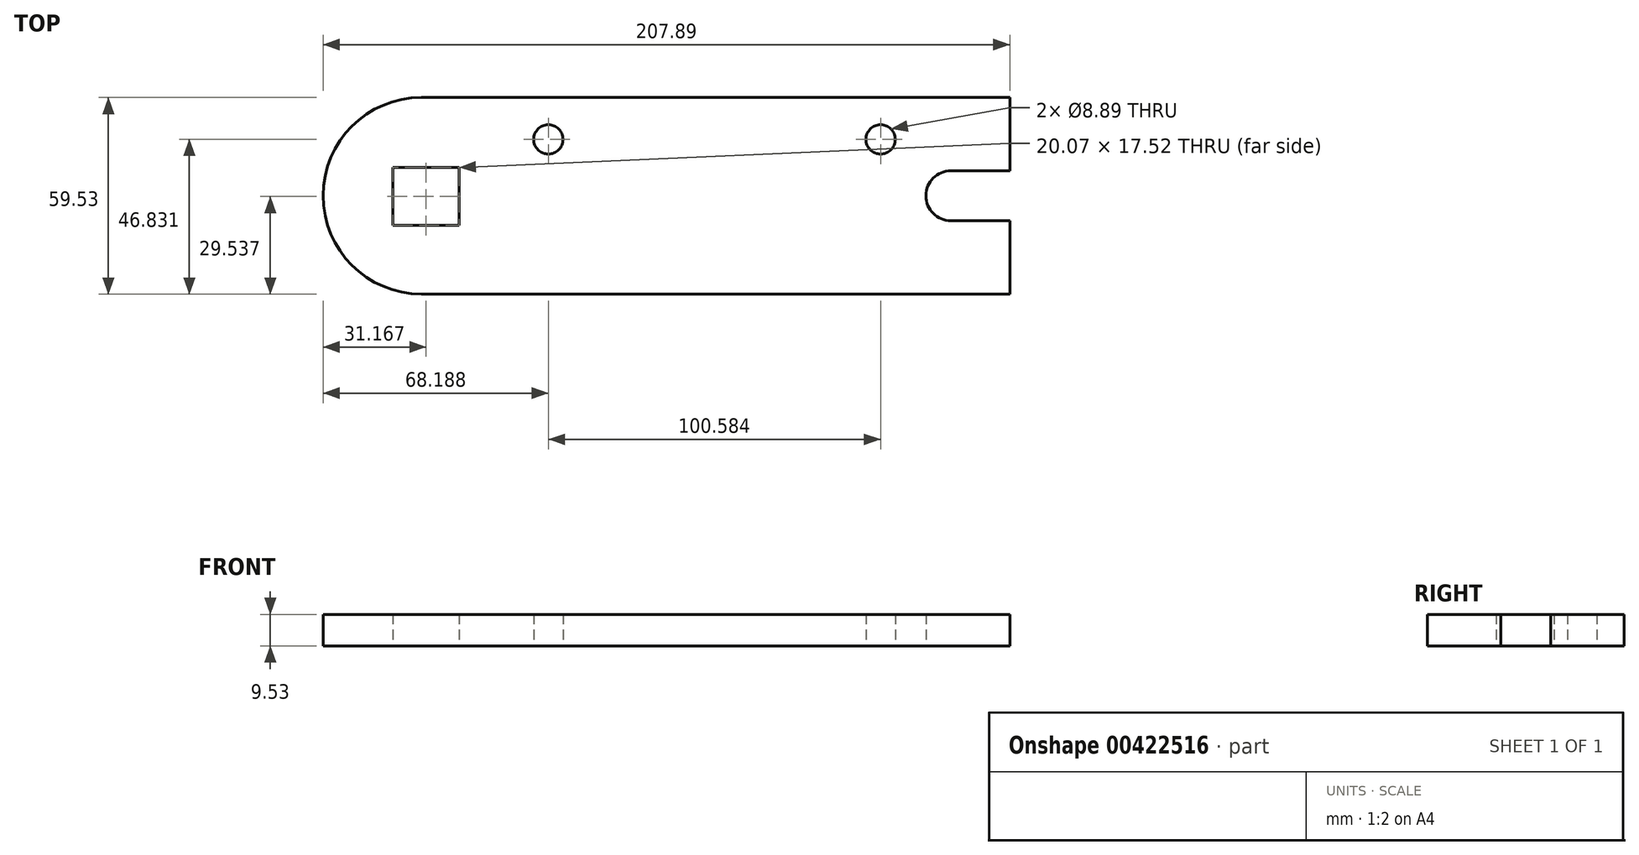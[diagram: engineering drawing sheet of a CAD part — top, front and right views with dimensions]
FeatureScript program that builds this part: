
annotation { "Feature Type Name" : "Feature", "Feature Type Description" : "" }
export const myFeature = defineFeature(function(context is Context, id is Id, definition is map)
    precondition{}
    {
        {
            var Q0;
            Q0=qCreatedBy(makeId("Top.planeOp"),FACE);
            var sketch = newSketch(context, id + "F0", { "sketchPlane" : qUnion([Q0])});
            skLineSegment(sketch, "E0.bottom", {"start": v(0, 0) * mm, "end": v(178.12, 0) * mm});
            skLineSegment(sketch, "E0.top", {"start": v(0, 59.53) * mm, "end": v(178.12, 59.53) * mm});
            skLineSegment(sketch, "E0.right", {"start": v(178.12, 0) * mm, "end": v(178.12, 22.23) * mm});
            skArc(sketch, "E1", {"start": v(0, 59.53) * mm, "mid": v(-29.77, 29.77) * mm, "end": v(0, 0) * mm});
            skLineSegment(sketch, "E2", {"start": v(178.12, 22.23) * mm, "end": v(160.26, 22.23) * mm});
            skLineSegment(sketch, "E3", {"start": v(178.12, 37.3) * mm, "end": v(160.26, 37.3) * mm});
            skArc(sketch, "E4", {"start": v(160.26, 37.3) * mm, "mid": v(152.72, 29.77) * mm, "end": v(160.26, 22.22) * mm});
            skPoint(sketch, "E5.end.orphan", {"position": v(152.72, 29.77) * mm});
            skLineSegment(sketch, "E6", {"start": v(178.12, 46.83) * mm, "end": v(139, 46.83) * mm, "construction": true});
            skCircle(sketch, "E7", {"center": v(139, 46.83) * mm, "radius": 4.45 * mm});
            skLineSegment(sketch, "E8", {"start": v(178.12, 46.83) * mm, "end": v(38.42, 46.83) * mm, "construction": true});
            skCircle(sketch, "E9", {"center": v(38.42, 46.83) * mm, "radius": 4.45 * mm});
            skLineSegment(sketch, "E10.trimOffspring", {"start": v(178.12, 37.3) * mm, "end": v(178.12, 59.53) * mm});
            skLineSegment(sketch, "E11", {"start": v(178.12, 37.3) * mm, "end": v(11.43, 37.3) * mm, "construction": true});
            skLineSegment(sketch, "E12.bottom", {"start": v(11.43, 38.3) * mm, "end": v(-8.64, 38.3) * mm});
            skLineSegment(sketch, "E12.top", {"start": v(11.43, 20.78) * mm, "end": v(-8.64, 20.78) * mm});
            skLineSegment(sketch, "E12.right", {"start": v(-8.64, 38.3) * mm, "end": v(-8.64, 20.78) * mm});
            skLineSegment(sketch, "E13", {"start": v(11.43, 38.3) * mm, "end": v(11.43, 20.78) * mm});
            skSolve(sketch);
        }
        {
            var Q0;
            Q0 = qSketchRegion(id + "F0", true);
            extrude(context, id + "F1", {"entities" : qUnion([Q0]), "depth" : 9.52 * mm});
        }
    });
